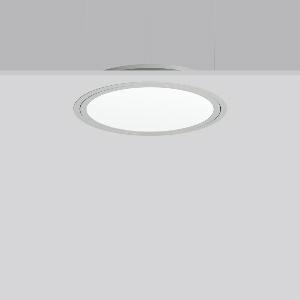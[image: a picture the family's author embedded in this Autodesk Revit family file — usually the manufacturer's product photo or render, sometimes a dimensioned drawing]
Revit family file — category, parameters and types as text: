
# Revit family: triona_round_e_312419_004_12_355e
name_source: partatom
category: Lighting Fixtures
units: mm (PartAtom-declared; Revit-internal decimal feet)

## family parameters
Cut with Voids When Loaded = No
Host = Face
Light Source = No
Part Type = Normal
Room Calculation Point = No
Round Connector Dimension = Use Diameter
Shared = No

## types (1)
- TRIONA round E (1 x LED Modul 830, 4650 lm, 3000)
    Apparent Load = 48 VA
    CIE Flux Codes = 49 80 96 100 100
    Color Rendering = 80
    Color Temperature = 3000
    Default Elevation = 1800 mm
    Description = Series: TRIONA round
Decorative round LED recessed surface luminaire. Cover made of sheet steel, powder-coated. Frame made of aluminium, powder-coated. Recessed ring: aluminium extrusion profile, powder coated. Light emission through a diffuser: plastic, opal. Lightguide and diffuser made of non-yellowing plastic (PMMA). Lateral light emission (RZB SIDELITE technology) for above-average homogeneous light distribution. Suitable for installation in cavity ceilings. Tool-free mounting system thanks to the rocker arm mechanism (patent pending). Electronic ballast included. Very easy installation thanks to Plug+Play connection. 
Colour: silver, matt (approx. RAL 9006)
Diameter: 505 mm
Height: 2 mm
Cut-out diameter: 482 mm
Recess height: 100 mm
Luminaire: recess height: 89 mm
Lamp: LED
Socket: without socket
Colour temperature: 3000K
Colour rendering index (CRI): 80
System power: 48 W
Rated luminous flux: 4650 lm
Luminous efficiency: 97 lm/W
Control gear: Converter, dimmable, DALI
Protection class: I
Type of protection: IP 40
    Height = 0 mm  [stored 0 ft]
    Lamp = 1 x LED Modul 830
    Lamp Light Flux = 4650 lm
    Lamp count = 1
    Length = 505 mm
    Lifetime = 50000 h
    Luminous efficacy = 97 lm/W
    Manufacturer = RZB
    ModVariant = No
    Model = 312419.004.12
    Mounting Place = Ceiling
    Mounting Type = Recessed
    Number of Poles = 1
    OnlyDefault = Yes
    Power Factor = 1
    Product Name = TRIONA round E
    Product group = Recessed modular luminaires
    ProductGroupID = 406
    Protection Class = Protection class I
    Protection Degree = IP 20
    RLX_Detail_Level = 1
    RLX_Emergency_Light_Flux = 0 lm
    RLX_Emergency_Type = 0
    RLX_Emergency_Type_DB = No
    RlxData = <blob elided: 31085 chars, md5=bd2fd19e>
    Socket = socket
    Standby Power = 0 W
    System Light Flux = 4650 lm
    System Power = 48 W
    Type Comments = Product without accessories
    Type Image = 312419.004.12.jpg
    URL = http://relux.com
    VarID = ---
    Voltage = 230 V
    Voltage Range = 220-240 V
    Weight = 0.00 kg
    Width = 0 mm  [stored 0 ft]

note: [stored X ft] marks values corroborated as IEEE doubles in the binary element streams (Revit-internal decimal feet)

## geometry (parser evidence)
native form markers: Blend x4, Sweep x10
no freeform markers — native parametric forms only
